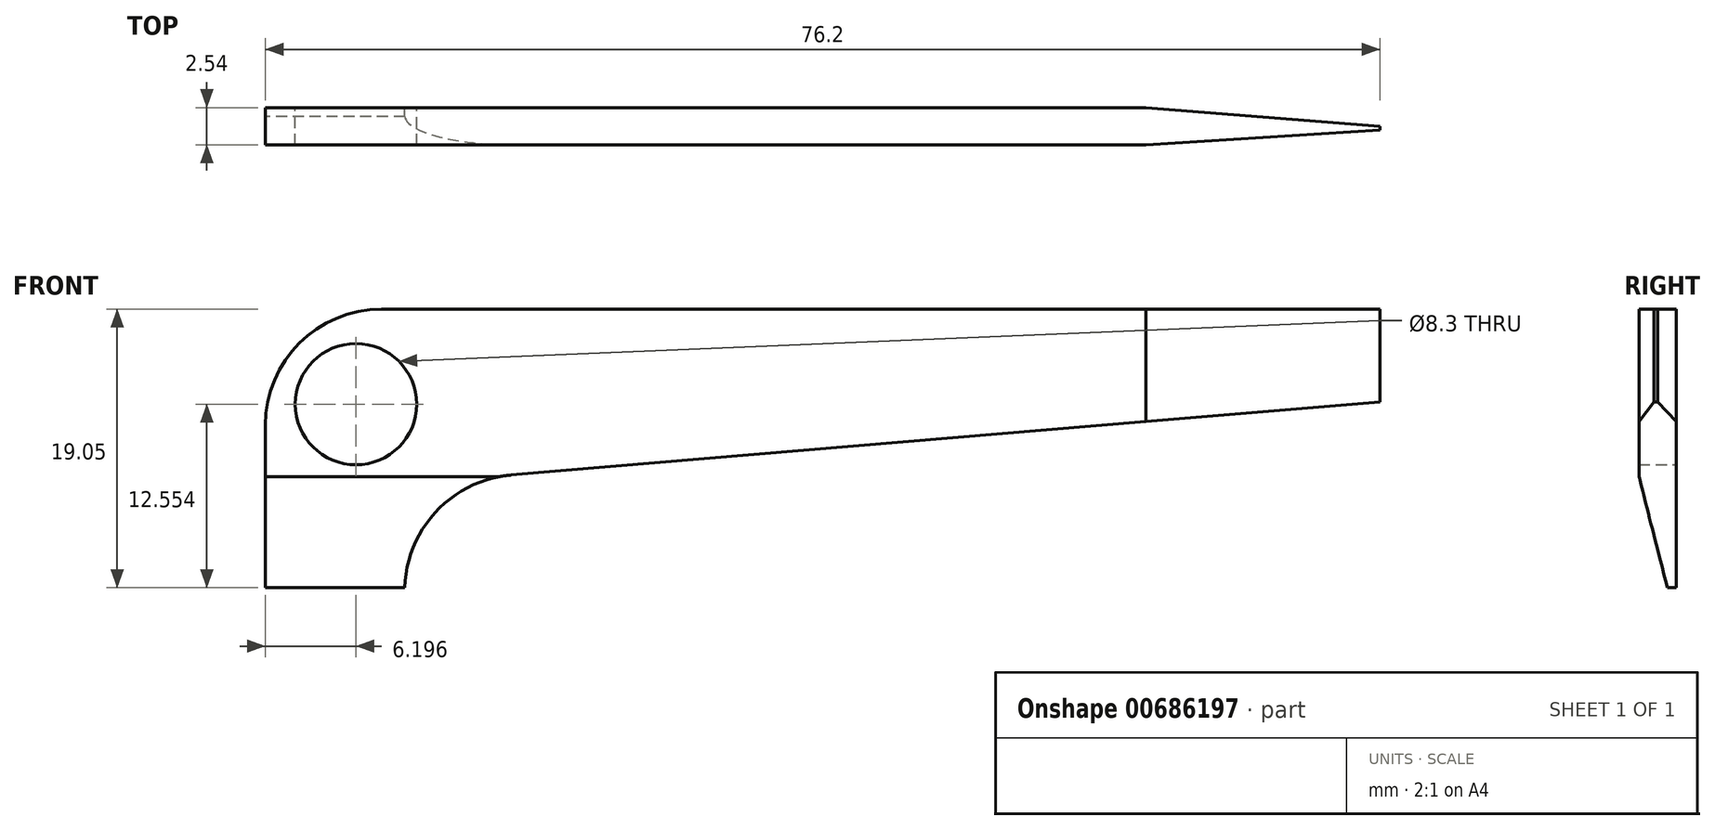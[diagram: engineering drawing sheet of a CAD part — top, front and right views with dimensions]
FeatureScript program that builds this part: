
annotation { "Feature Type Name" : "Feature", "Feature Type Description" : "" }
export const myFeature = defineFeature(function(context is Context, id is Id, definition is map)
    precondition{}
    {
        {
            var Q0;
            Q0=qCreatedBy(makeId("Front.planeOp"),FACE);
            var sketch = newSketch(context, id + "F0", { "sketchPlane" : qUnion([Q0])});
            skLineSegment(sketch, "E0", {"start": v(-9.52, -4.4) * mm, "end": v(-9.52, 6.7) * mm});
            skLineSegment(sketch, "E1", {"start": v(-1.59, 14.64) * mm, "end": v(66.67, 14.64) * mm});
            skLineSegment(sketch, "E2", {"start": v(66.67, 14.64) * mm, "end": v(66.67, 8.3) * mm});
            skLineSegment(sketch, "E3", {"start": v(66.68, 8.3) * mm, "end": v(7.27, 3.3) * mm});
            skLineSegment(sketch, "E4", {"start": v(0, -4.4) * mm, "end": v(0, -4.62) * mm});
            skLineSegment(sketch, "E5", {"start": v(0, -4.4) * mm, "end": v(-9.52, -4.4) * mm});
            skPoint(sketch, "E6.visualSharp", {"position": v(0, 2.68) * mm});
            skArc(sketch, "E6.filletArc", {"start": v(7.27, 3.3) * mm, "mid": v(2.1, 0.76) * mm, "end": v(0, -4.62) * mm});
            skCircle(sketch, "E7", {"center": v(-3.33, 8.14) * mm, "radius": 4.15 * mm});
            skPoint(sketch, "E8.visualSharp", {"position": v(-9.52, 14.64) * mm});
            skArc(sketch, "E8.filletArc", {"start": v(-1.59, 14.64) * mm, "mid": v(-7.2, 12.32) * mm, "end": v(-9.52, 6.7) * mm});
            skSolve(sketch);
        }
        {
            var Q0;
            Q0=makeQuery(id+"F0.imprint","IMPRINT",FACE,{"disambiguationData":[TD([[makeQuery(id+"F0.imprint","IMPRINT",EDGE,{"derivedFrom":sQuery(id+"F0.wireOp",EDGE,"E0")}),-1.0]])]});
            extrude(context, id + "F1", {"entities" : qUnion([Q0]), "depth" : 2.54 * mm, "offsetDistance" : 25.4 * mm});
        }
        {
            var Q0;
            Q0=makeQuery(id+"F1.opExtrude","SWEPT_FACE",FACE,{"disambiguationData":[OSD([sQuery(id+"F0.wireOp",EDGE,"E0")])]});
            var sketch = newSketch(context, id + "F2", { "sketchPlane" : qUnion([Q0])});
            skLineSegment(sketch, "E9", {"start": v(2.54, 3.2) * mm, "end": v(0.6, -4.4) * mm});
            skLineSegment(sketch, "E10", {"start": v(0.6, -4.4) * mm, "end": v(0, -4.4) * mm});
            skLineSegment(sketch, "E11", {"start": v(0, -4.4) * mm, "end": v(0, 3.23) * mm});
            skSolve(sketch);
        }
        {
            var Q0;
            {var subQ0=sQuery(id+"F2.wireOp",EDGE,"E9");Q0=makeQuery(id+"F2.imprint","IMPRINT",FACE,{"disambiguationData":[TD([[makeQuery(id+"F2.imprint","IMPRINT",EDGE,{"derivedFrom":subQ0}),1.0]])]});}
            extrude(context, id + "F3", {"entities" : qUnion([Q0]), "operationType" : NewBodyOperationType.REMOVE, "oppositeDirection" : true, "depth" : 25.4 * mm, "offsetDistance" : 25.4 * mm});
        }
        {
            var Q0;
            Q0=makeQuery(id+"F1.opExtrude","SWEPT_FACE",FACE,{"disambiguationData":[OSD([sQuery(id+"F0.wireOp",EDGE,"E4")])]});
            extrude(context, id + "F4", {"entities" : qUnion([Q0]), "operationType" : NewBodyOperationType.REMOVE, "oppositeDirection" : true, "depth" : 25.4 * mm, "offsetDistance" : 25.4 * mm});
        }
        {
            var Q0;
            Q0=makeQuery(id+"F1.opExtrude","SWEPT_FACE",FACE,{"disambiguationData":[OSD([sQuery(id+"F0.wireOp",EDGE,"E1")])]});
            var sketch = newSketch(context, id + "F5", { "sketchPlane" : qUnion([Q0])});
            skLineSegment(sketch, "E12", {"start": v(50.66, 2.25) * mm, "end": v(50.66, -5.77) * mm});
            skLineSegment(sketch, "E13", {"start": v(50.66, 0) * mm, "end": v(66.67, -1.27) * mm});
            skLineSegment(sketch, "E14", {"start": v(66.67, -1.27) * mm, "end": v(66.67, -1.52) * mm});
            skLineSegment(sketch, "E15", {"start": v(66.67, -1.52) * mm, "end": v(50.66, -2.54) * mm});
            skSolve(sketch);
        }
        {
            var Q0;
            {var subQ0=sQuery(id+"F5.wireOp",EDGE,"E13");Q0=makeQuery(id+"F5.imprint","IMPRINT",FACE,{"disambiguationData":[TD([[makeQuery(id+"F5.imprint","IMPRINT",EDGE,{"derivedFrom":subQ0}),1.0]])]});}
            var Q1;
            {var subQ0=sQuery(id+"F5.wireOp",EDGE,"E15");Q1=makeQuery(id+"F5.imprint","IMPRINT",FACE,{"disambiguationData":[TD([[makeQuery(id+"F5.imprint","IMPRINT",EDGE,{"derivedFrom":subQ0}),1.0]])]});}
            extrude(context, id + "F6", {"entities" : qUnion([Q0, Q1]), "operationType" : NewBodyOperationType.REMOVE, "oppositeDirection" : true, "depth" : 25.4 * mm, "offsetDistance" : 25.4 * mm});
        }
    });
